# Revit family: NLRS_57_DUF_UN_rechthoekig-haaks-T-stuk-nijburg
name_source: partatom
category: Duct Fittings
units: mm (PartAtom-declared; Revit-internal decimal feet)

## family parameters
Always vertical = Yes
Cut with Voids When Loaded = No
Part Type = Tee
Round Connector Dimension = Use Diameter
Shared = No
Work Plane-Based = No

## types (1)
- T-stuk haaks
    Assembly Code = 57.50
    Default Elevation = 0 mm  [stored 0 ft]
    Description = Rechthoekig haaks T-stuk
    Manufacturer = Nijburg Klimaattechniek BV
    Model = T-stuk haaks
    NLRS_C_content_datum_gewijzigd = 05-05-2023
    NLRS_C_content_provider = Nijburg Klimaattechniek
    NLRS_C_content_versie = 1.20.00
    NLRS_C_description = Rechthoekig haaks T-stuk
    NLRS_C_model = T-stuk haaks
    NPR_Artikelcode = RHKV
    URL = https://nijburg-klimaattechniek.nl

note: [stored X ft] marks values corroborated as IEEE doubles in the binary element streams (Revit-internal decimal feet)

## geometry (parser evidence)
native form markers: Sweep x3
no freeform markers — native parametric forms only
